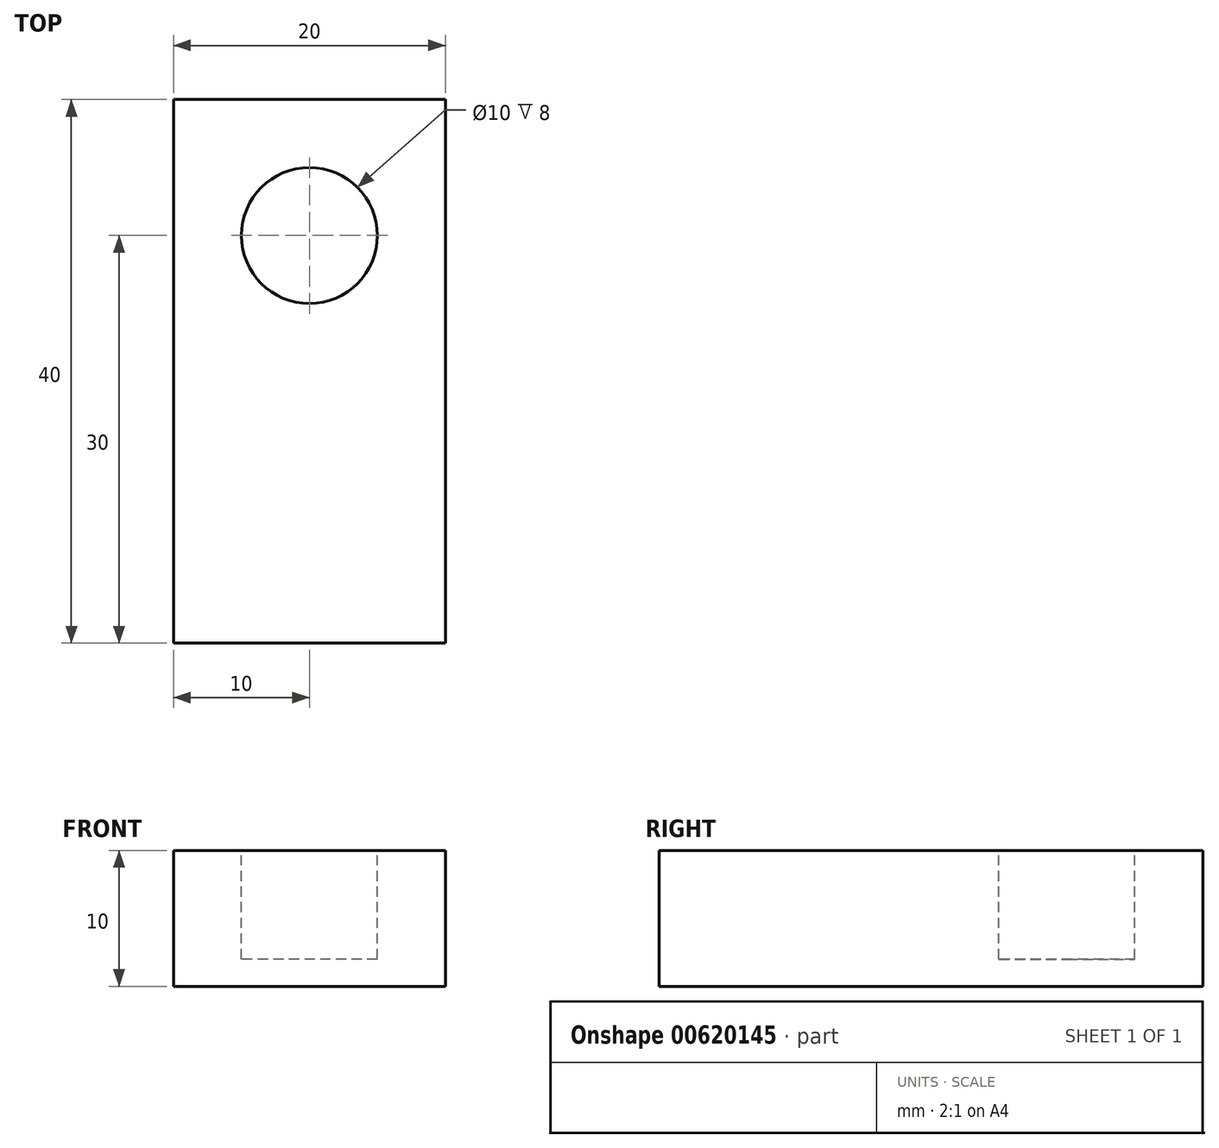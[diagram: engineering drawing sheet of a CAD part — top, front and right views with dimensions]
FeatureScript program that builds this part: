
annotation { "Feature Type Name" : "Feature", "Feature Type Description" : "" }
export const myFeature = defineFeature(function(context is Context, id is Id, definition is map)
    precondition{}
    {
        {
            var Q0;
            Q0=qCreatedBy(makeId("Front.planeOp"),FACE);
            var sketch = newSketch(context, id + "F0", { "sketchPlane" : qUnion([Q0])});
            skLineSegment(sketch, "E0.bottom", {"start": v(-10, 0) * mm, "end": v(10, 0) * mm});
            skLineSegment(sketch, "E0.top", {"start": v(-10, 10) * mm, "end": v(10, 10) * mm});
            skLineSegment(sketch, "E0.left", {"start": v(-10, 0) * mm, "end": v(-10, 10) * mm});
            skLineSegment(sketch, "E0.right", {"start": v(10, 0) * mm, "end": v(10, 10) * mm});
            skSolve(sketch);
        }
        {
            var Q0;
            Q0 = qSketchRegion(id + "F0", true);
            extrude(context, id + "F1", {"entities" : qUnion([Q0]), "depth" : 30 * mm, "offsetDistance" : 25 * mm});
        }
        {
            var Q0;
            Q0=makeQuery(id+"F1.opExtrude","CAP_FACE",FACE,{"disambiguationData":[OSD([sQuery(id+"F0.wireOp",EDGE,"E0.bottom"),sQuery(id+"F0.wireOp",EDGE,"E0.top"),sQuery(id+"F0.wireOp",EDGE,"E0.left"),sQuery(id+"F0.wireOp",EDGE,"E0.right")])],"isStart":true});
            extrude(context, id + "F2", {"entities" : qUnion([Q0]), "operationType" : NewBodyOperationType.ADD, "depth" : 10 * mm, "offsetDistance" : 25 * mm});
        }
        {
            var Q0;
            {var subQ0=sQuery(id+"F0.wireOp",EDGE,"E0.top");Q0=makeQuery(id+"F2.boolean.opBoolean","MERGE",FACE,{"derivedFrom":[makeQuery(id+"F1.opExtrude","SWEPT_FACE",FACE,{"disambiguationData":[OSD([subQ0])]}),makeQuery(id+"F2.opExtrude","SWEPT_FACE",FACE,{"disambiguationData":[OSD([subQ0])]})]});}
            var sketch = newSketch(context, id + "F3", { "sketchPlane" : qUnion([Q0])});
            skSolve(sketch);
        }
        {
            var Q0;
            {var subQ0=sQuery(id+"F0.wireOp",EDGE,"E0.top");Q0=makeQuery(id+"F3.imprint","IMPRINT",FACE,{"disambiguationData":[TD([[makeQuery(id+"F3.imprint","IMPRINT",EDGE,{"derivedFrom":makeQuery(id+"F1.opExtrude","CAP_EDGE",EDGE,{"disambiguationData":[OSD([subQ0])],"isStart":false})}),1.0]])]});}
            var sketch = newSketch(context, id + "F4", { "sketchPlane" : qUnion([Q0])});
            skCircle(sketch, "E1", {"center": v(0, 0) * mm, "radius": 5 * mm});
            skSolve(sketch);
        }
        {
            var Q0;
            Q0 = qSketchRegion(id + "F4", true);
            extrude(context, id + "F5", {"entities" : qUnion([Q0]), "operationType" : NewBodyOperationType.REMOVE, "oppositeDirection" : true, "depth" : 8 * mm, "offsetDistance" : 25 * mm});
        }
    });
